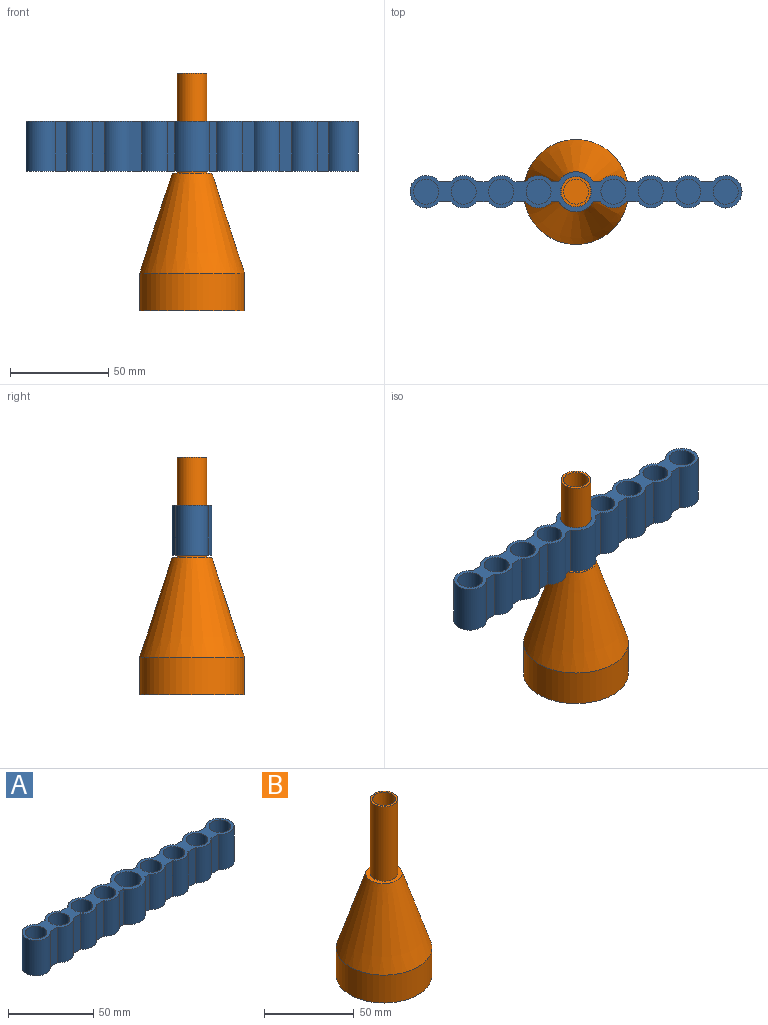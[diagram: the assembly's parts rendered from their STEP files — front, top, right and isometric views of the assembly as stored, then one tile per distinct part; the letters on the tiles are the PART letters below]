
ASSEMBLY  parts=2 mates=1
PART A: 51 faces, bbox 168.9x20.3x25.4 mm
  f0: plane 168.91x20.32mm, normal (0,0,1), area 1089.5mm2, adj f1,f2,f3,f4,f5,f6,f7,f8
  f1: cylinder r=8.26mm len=25.4mm, axis (0,0,-1), area 1039.5mm2, adj f0,f2,f32,f34
  f2: plane 25.4x6.04mm, normal (0,1,0), area 153.3mm2, adj f0,f1,f3,f34
  f3: cylinder r=8.26mm len=25.4mm, axis (0,0,-1), area 380.7mm2, adj f0,f2,f4,f34
  f4: plane 25.4x6.04mm, normal (0,1,0), area 153.3mm2, adj f0,f3,f5,f34
  f5: cylinder r=8.26mm len=25.4mm, axis (0,0,-1), area 380.7mm2, adj f0,f4,f6,f34
  f6: plane 25.4x6.04mm, normal (0,1,0), area 153.3mm2, adj f0,f5,f7,f34
  f7: cylinder r=8.26mm len=25.4mm, axis (0,0,-1), area 380.7mm2, adj f0,f6,f8,f34
  f8: plane 25.4x3.74mm, normal (0,1,0), area 95.1mm2, adj f0,f7,f9,f34
  f9: cylinder r=10.16mm len=25.4mm, axis (0,0,-1), area 540.5mm2, adj f0,f8,f10,f34
  f10: plane 25.4x3.74mm, normal (0,1,0), area 95.1mm2, adj f0,f9,f11,f34
  f11: cylinder r=8.26mm len=25.4mm, axis (0,0,-1), area 380.7mm2, adj f0,f10,f12,f34
  f12: plane 25.4x6.04mm, normal (0,1,0), area 153.3mm2, adj f0,f11,f13,f34
  f13: cylinder r=8.26mm len=25.4mm, axis (0,0,-1), area 380.7mm2, adj f0,f12,f14,f34
  f14: plane 25.4x6.04mm, normal (0,1,0), area 153.3mm2, adj f0,f13,f15,f34
  f15: cylinder r=8.26mm len=25.4mm, axis (0,0,-1), area 380.7mm2, adj f0,f14,f16,f34
  f16: plane 25.4x6.04mm, normal (0,1,0), area 153.3mm2, adj f0,f15,f17,f34
  f17: cylinder r=8.26mm len=25.4mm, axis (0,0,-1), area 1039.5mm2, adj f0,f16,f18,f34
  f18: plane 25.4x6.04mm, normal (0,-1,0), area 153.3mm2, adj f0,f17,f19,f34
  f19: cylinder r=8.26mm len=25.4mm, axis (0,0,-1), area 380.7mm2, adj f0,f18,f20,f34
  f20: plane 25.4x6.04mm, normal (0,-1,0), area 153.3mm2, adj f0,f19,f21,f34
  f21: cylinder r=8.26mm len=25.4mm, axis (0,0,-1), area 380.7mm2, adj f0,f20,f22,f34
  f22: plane 25.4x6.04mm, normal (0,-1,0), area 153.3mm2, adj f0,f21,f23,f34
  f23: cylinder r=8.26mm len=25.4mm, axis (0,0,-1), area 380.7mm2, adj f0,f22,f24,f34
  f24: plane 25.4x3.74mm, normal (0,-1,0), area 95.1mm2, adj f0,f23,f25,f34
  f25: cylinder r=10.16mm len=25.4mm, axis (0,0,-1), area 540.5mm2, adj f0,f24,f26,f34
  f26: plane 25.4x3.74mm, normal (0,-1,0), area 95.1mm2, adj f0,f25,f27,f34
  f27: cylinder r=8.26mm len=25.4mm, axis (0,0,-1), area 380.7mm2, adj f0,f26,f28,f34
  f28: plane 25.4x6.04mm, normal (0,-1,0), area 153.3mm2, adj f0,f27,f29,f34
  f29: cylinder r=8.26mm len=25.4mm, axis (0,0,-1), area 380.7mm2, adj f0,f28,f30,f34
  f30: plane 25.4x6.04mm, normal (0,-1,0), area 153.3mm2, adj f0,f29,f31,f34
  f31: cylinder r=8.26mm len=25.4mm, axis (0,0,-1), area 380.7mm2, adj f0,f30,f32,f34
  f32: plane 25.4x6.04mm, normal (0,-1,0), area 153.3mm2, adj f0,f1,f31,f34
  f33: cylinder r=7.77mm len=25.4mm, axis (0,0,-1), area 1240.4mm2, adj f0,f34
  f34: plane 168.91x20.32mm, normal (0,0,-1), area 2102.9mm2, adj f1,f2,f3,f4,f5,f6,f7,f8
  f35: cylinder r=6.35mm len=15.24mm, axis (0,0,1), area 608mm2, adj f0,f36
  f36: plane 12.7x12.7mm, normal (0,0,1), area 126.7mm2, adj f35
  f37: cylinder r=6.35mm len=15.24mm, axis (0,0,1), area 608mm2, adj f0,f38
  f38: plane 12.7x12.7mm, normal (0,0,1), area 126.7mm2, adj f37
  f39: cylinder r=6.35mm len=15.24mm, axis (0,0,1), area 608mm2, adj f0,f40
  f40: plane 12.7x12.7mm, normal (0,0,1), area 126.7mm2, adj f39
  f41: cylinder r=6.35mm len=15.24mm, axis (0,0,1), area 608mm2, adj f0,f42
  f42: plane 12.7x12.7mm, normal (0,0,1), area 126.7mm2, adj f41
  f43: cylinder r=6.35mm len=15.24mm, axis (0,0,1), area 608mm2, adj f0,f44
  f44: plane 12.7x12.7mm, normal (0,0,1), area 126.7mm2, adj f43
  f45: cylinder r=6.35mm len=15.24mm, axis (0,0,1), area 608mm2, adj f0,f46
  f46: plane 12.7x12.7mm, normal (0,0,1), area 126.7mm2, adj f45
  f47: cylinder r=6.35mm len=15.24mm, axis (0,0,1), area 608mm2, adj f0,f48
  f48: plane 12.7x12.7mm, normal (0,0,1), area 126.7mm2, adj f47
  f49: cylinder r=6.35mm len=15.24mm, axis (0,0,1), area 608mm2, adj f0,f50
  f50: plane 12.7x12.7mm, normal (0,0,1), area 126.7mm2, adj f49
PART B: 8 faces, bbox 53.3x53.3x120.7 mm
  f0: cylinder r=26.67mm len=53.34mm, axis (0,0,-1), area 3192.3mm2, adj f1,f3
  f1: plane 53.34x53.34mm, normal (0,0,-1), area 2234.6mm2, adj f0
  f2: plane 20.32x20.32mm, normal (0,0,1), area 141.9mm2, adj f3,f4
  f3: cone r=10.16mm half-angle=18deg, axis (0,0,-1), area 6180.4mm2, adj f0,f2
  f4: cylinder r=7.62mm len=50.8mm, axis (0,0,-1), area 2432.2mm2, adj f2,f5
  f5: plane 15.24x15.24mm, normal (0,0,1), area 55.7mm2, adj f4,f6
  f6: cylinder r=6.35mm len=15.24mm, axis (0,0,1), area 608mm2, adj f5,f7
  f7: plane 12.7x12.7mm, normal (0,0,1), area 126.7mm2, adj f6
PLACE A t=(-57.27,21.6,44.02)mm
PLACE B t=(-57.27,21.6,-26.82)mm
MATE slider A.f33 <-> B.f4  axis (0,0,-1) through (-57.27,21.6,69.42)mm
